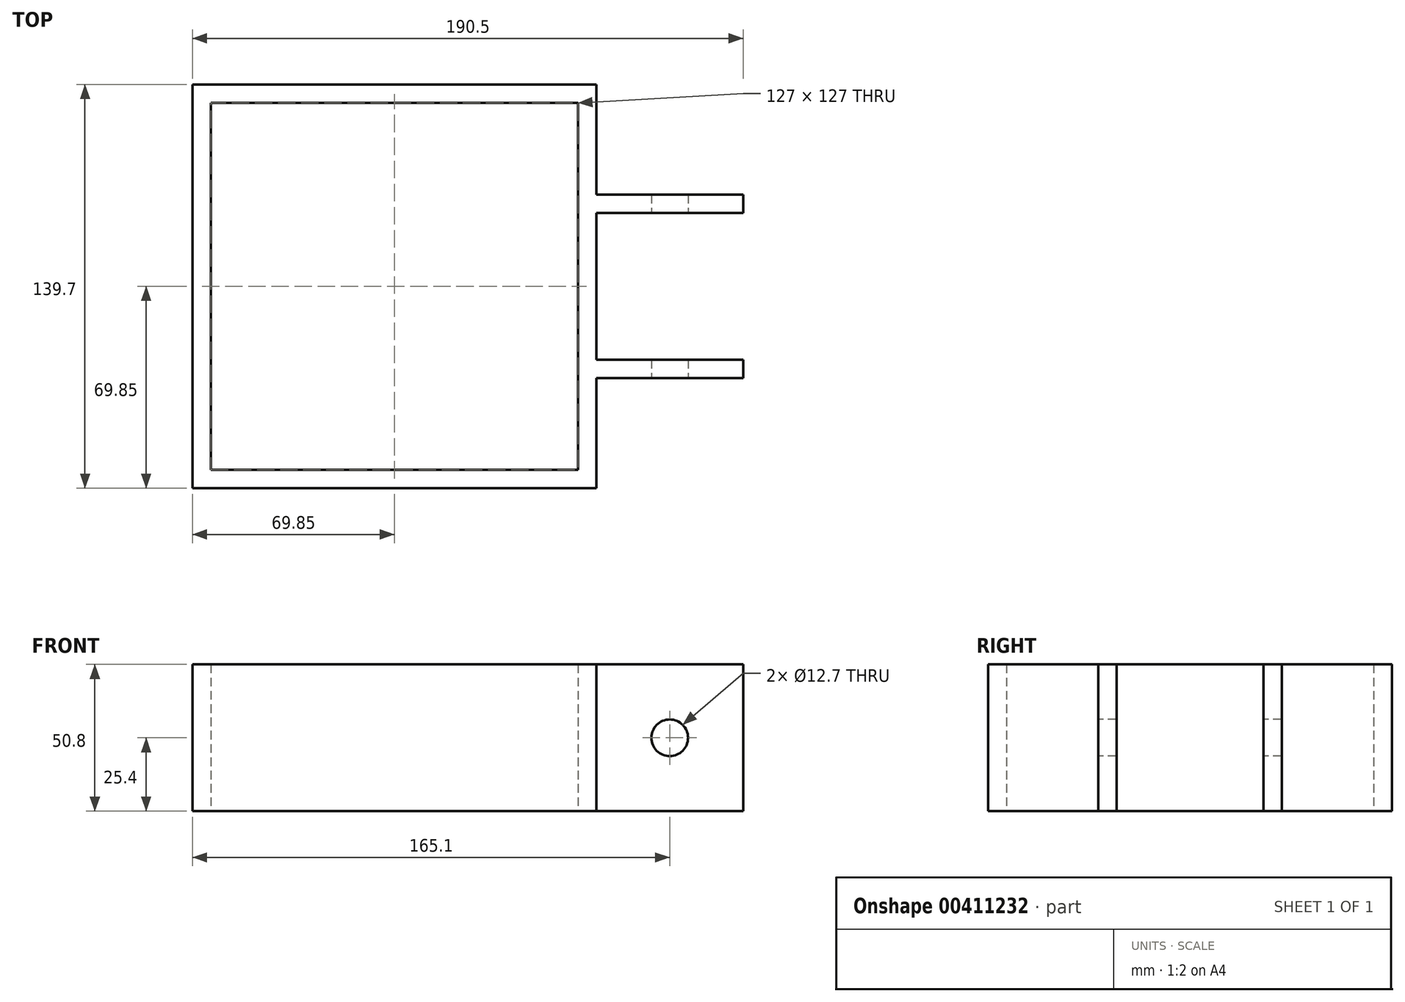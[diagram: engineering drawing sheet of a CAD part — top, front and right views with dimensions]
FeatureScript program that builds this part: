
annotation { "Feature Type Name" : "Feature", "Feature Type Description" : "" }
export const myFeature = defineFeature(function(context is Context, id is Id, definition is map)
    precondition{}
    {
        {
            var Q0;
            Q0=qCreatedBy(makeId("Top.planeOp"),FACE);
            var sketch = newSketch(context, id + "F0", { "sketchPlane" : qUnion([Q0])});
            skLineSegment(sketch, "E0.bottom", {"start": v(69.85, -69.85) * mm, "end": v(-69.85, -69.85) * mm});
            skLineSegment(sketch, "E0.top", {"start": v(69.85, 69.85) * mm, "end": v(-69.85, 69.85) * mm});
            skLineSegment(sketch, "E0.left", {"start": v(69.85, -69.85) * mm, "end": v(69.85, 69.85) * mm});
            skLineSegment(sketch, "E0.right", {"start": v(-69.85, -69.85) * mm, "end": v(-69.85, 69.85) * mm});
            skPoint(sketch, "E0.middle", {"position": v(0, 0) * mm});
            skLineSegment(sketch, "E1.bottom", {"start": v(63.5, -63.5) * mm, "end": v(-63.5, -63.5) * mm});
            skLineSegment(sketch, "E1.top", {"start": v(63.5, 63.5) * mm, "end": v(-63.5, 63.5) * mm});
            skLineSegment(sketch, "E1.left", {"start": v(63.5, -63.5) * mm, "end": v(63.5, 63.5) * mm});
            skLineSegment(sketch, "E1.right", {"start": v(-63.5, -63.5) * mm, "end": v(-63.5, 63.5) * mm});
            skPoint(sketch, "E2", {"position": v(69.85, -25.4) * mm});
            skPoint(sketch, "E3", {"position": v(69.85, 25.4) * mm});
            skPoint(sketch, "E4", {"position": v(69.85, 0) * mm});
            skLineSegment(sketch, "E5.bottom", {"start": v(69.85, 25.4) * mm, "end": v(120.65, 25.4) * mm});
            skLineSegment(sketch, "E5.top", {"start": v(69.85, 31.75) * mm, "end": v(120.65, 31.75) * mm});
            skLineSegment(sketch, "E5.left", {"start": v(69.85, 25.4) * mm, "end": v(69.85, 31.75) * mm});
            skLineSegment(sketch, "E5.right", {"start": v(120.65, 25.4) * mm, "end": v(120.65, 31.75) * mm});
            skLineSegment(sketch, "E6.bottom", {"start": v(69.85, -25.4) * mm, "end": v(120.65, -25.4) * mm});
            skLineSegment(sketch, "E6.top", {"start": v(69.85, -31.75) * mm, "end": v(120.65, -31.75) * mm});
            skLineSegment(sketch, "E6.left", {"start": v(69.85, -25.4) * mm, "end": v(69.85, -31.75) * mm});
            skLineSegment(sketch, "E6.right", {"start": v(120.65, -25.4) * mm, "end": v(120.65, -31.75) * mm});
            skSolve(sketch);
        }
        {
            var Q0;
            Q0 = qSketchRegion(id + "F0", true);
            extrude(context, id + "F1", {"entities" : qUnion([Q0]), "depth" : 50.8 * mm});
        }
        {
            var Q0;
            Q0=makeQuery(id+"F1.opExtrude","SWEPT_FACE",FACE,{"disambiguationData":[OSD([sQuery(id+"F0.wireOp",EDGE,"E6.top")])]});
            var sketch = newSketch(context, id + "F2", { "sketchPlane" : qUnion([Q0])});
            skCircle(sketch, "E7", {"center": v(95.25, 25.4) * mm, "radius": 6.35 * mm});
            skSolve(sketch);
        }
        {
            var Q0;
            Q0=makeQuery(id+"F2.imprint","IMPRINT",FACE,{"disambiguationData":[TD([[makeQuery(id+"F2.imprint","IMPRINT",EDGE,{"derivedFrom":sQuery(id+"F2.wireOp",EDGE,"E7")}),1.0]])]});
            extrude(context, id + "F3", {"entities" : qUnion([Q0]), "operationType" : NewBodyOperationType.REMOVE, "endBound" : BoundingType.THROUGH_ALL, "oppositeDirection" : true, "depth" : 25 * mm});
        }
    });
